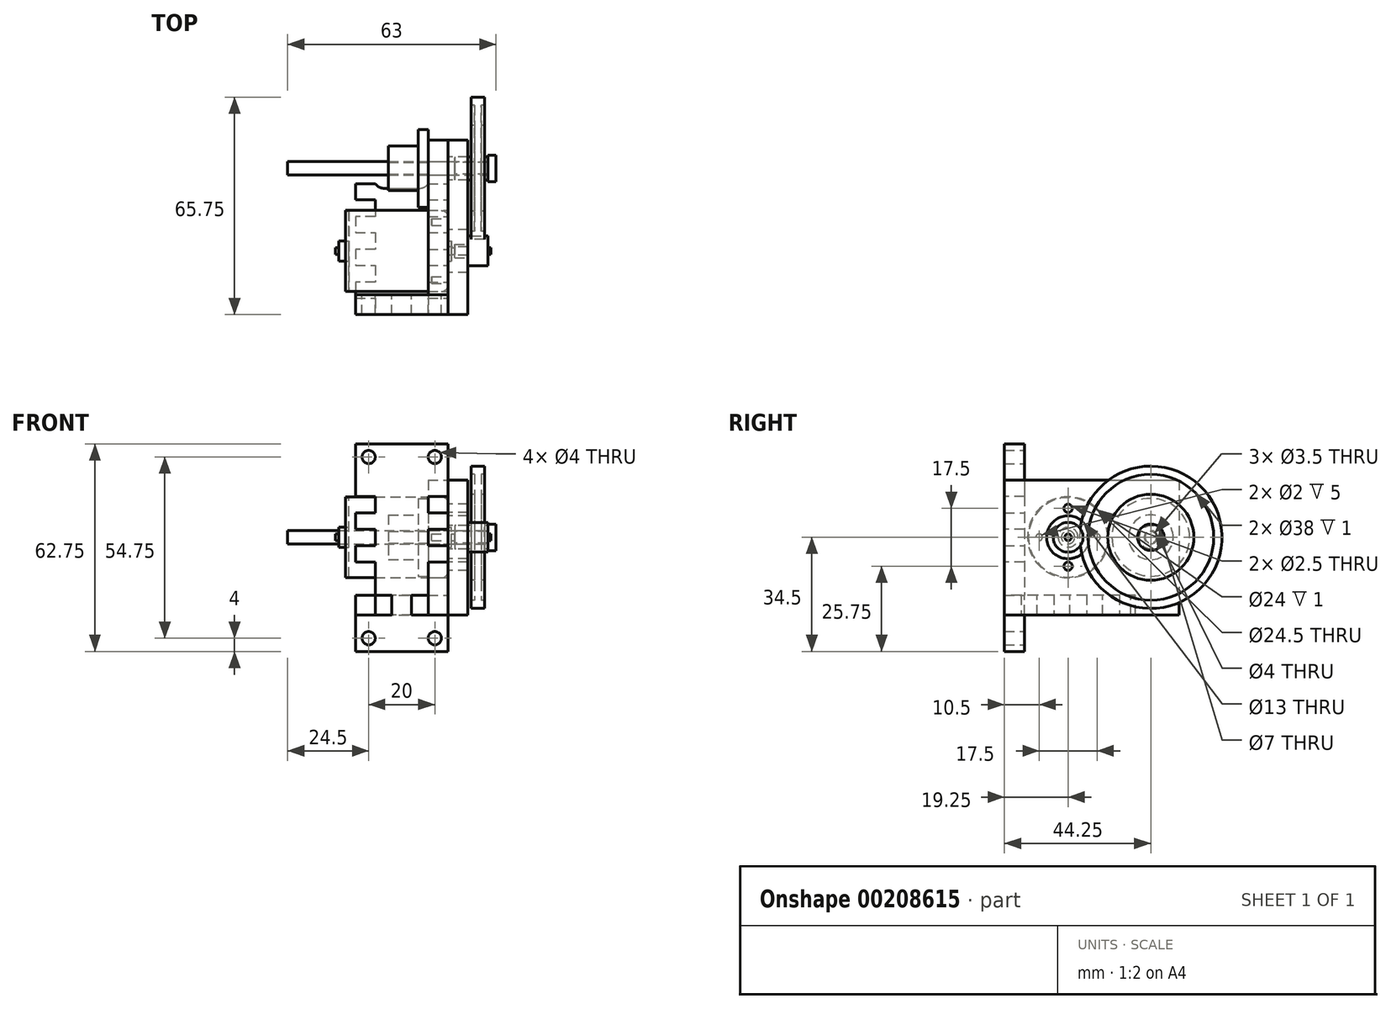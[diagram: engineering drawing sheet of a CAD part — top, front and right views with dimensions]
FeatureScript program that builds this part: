
annotation { "Feature Type Name" : "Feature", "Feature Type Description" : "" }
export const myFeature = defineFeature(function(context is Context, id is Id, definition is map)
    precondition{}
    {
        {
            assignVariable(context, id + "F0", {"name" : "ply", "anyValue" : 6});
        }
        {
            var Q0;
            Q0=qCreatedBy(makeId("Top.planeOp"),FACE);
            var sketch = newSketch(context, id + "F1", { "sketchPlane" : qUnion([Q0])});
            skLineSegment(sketch, "E0", {"start": v(0, 21.5) * mm, "end": v(2, 21.5) * mm});
            skLineSegment(sketch, "E1", {"start": v(2, 21.5) * mm, "end": v(2, 19) * mm});
            skLineSegment(sketch, "E2", {"start": v(2, 19) * mm, "end": v(1, 19) * mm});
            skLineSegment(sketch, "E3", {"start": v(1, 19) * mm, "end": v(1, 13) * mm});
            skLineSegment(sketch, "E4", {"start": v(1, 13) * mm, "end": v(2, 13) * mm});
            skLineSegment(sketch, "E5", {"start": v(2, 13) * mm, "end": v(2, 3.5) * mm});
            skLineSegment(sketch, "E6", {"start": v(2, 3.5) * mm, "end": v(3, 3.5) * mm});
            skLineSegment(sketch, "E7", {"start": v(3, 3.5) * mm, "end": v(3, 1.75) * mm});
            skLineSegment(sketch, "E8", {"start": v(3, 1.75) * mm, "end": v(0, 1.75) * mm});
            skLineSegment(sketch, "E9", {"start": v(0, 1.75) * mm, "end": v(0, 21.5) * mm, "construction": true});
            skLineSegment(sketch, "E10", {"start": v(0, 0) * mm, "end": v(6.26, 0) * mm, "construction": true});
            skLineSegment(sketch, "E11.MirrorCS", {"start": v(-7, 3.5) * mm, "end": v(-7, 1.75) * mm});
            skLineSegment(sketch, "E12.MirrorCS", {"start": v(0, 21.5) * mm, "end": v(-2, 21.5) * mm});
            skLineSegment(sketch, "E13.MirrorCS", {"start": v(-2, 21.5) * mm, "end": v(-2, 19) * mm});
            skLineSegment(sketch, "E14.MirrorCS", {"start": v(-2, 3.5) * mm, "end": v(-7, 3.5) * mm});
            skLineSegment(sketch, "E15.MirrorCS", {"start": v(-2, 19) * mm, "end": v(-1, 19) * mm});
            skLineSegment(sketch, "E16.MirrorCS", {"start": v(-2, 13) * mm, "end": v(-2, 3.5) * mm});
            skLineSegment(sketch, "E17.MirrorCS", {"start": v(-7, 1.75) * mm, "end": v(0, 1.75) * mm});
            skLineSegment(sketch, "E18.MirrorCS", {"start": v(-1, 19) * mm, "end": v(-1, 13) * mm});
            skLineSegment(sketch, "E19.MirrorCS", {"start": v(-1, 13) * mm, "end": v(-2, 13) * mm});
            skSolve(sketch);
        }
        {
            var Q0;
            Q0 = qSketchRegion(id + "F1", true);
            var Q1;
            Q1=sQuery(id+"F1.wireOp",EDGE,"E10");
            revolve(context, id + "F2", {"entities" : qUnion([Q0]), "axis" : qUnion([Q1]), "revolveType" : RevolveType.FULL});
        }
        {
            var Q0;
            Q0=qCreatedBy(makeId("Top.planeOp"),FACE);
            var sketch = newSketch(context, id + "F3", { "sketchPlane" : qUnion([Q0])});
            skLineSegment(sketch, "E20", {"start": v(-57.5, 2) * mm, "end": v(3, 2) * mm});
            skLineSegment(sketch, "E21", {"start": v(3, 2) * mm, "end": v(3, 4) * mm});
            skLineSegment(sketch, "E22", {"start": v(3, 4) * mm, "end": v(5.5, 4) * mm});
            skLineSegment(sketch, "E23", {"start": v(5.5, 4) * mm, "end": v(5.5, 0) * mm});
            skLineSegment(sketch, "E24", {"start": v(5.5, 0) * mm, "end": v(-57.5, 0) * mm});
            skLineSegment(sketch, "E25", {"start": v(-57.5, 0) * mm, "end": v(-57.5, 2) * mm});
            skSolve(sketch);
        }
        {
            var Q0;
            Q0 = qSketchRegion(id + "F3", true);
            var Q1;
            Q1=sQuery(id+"F3.wireOp",EDGE,"E24");
            revolve(context, id + "F4", {"entities" : qUnion([Q0]), "axis" : qUnion([Q1]), "revolveType" : RevolveType.FULL});
        }
        {
            var Q0;
            Q0=qCreatedBy(makeId("Top.planeOp"),FACE);
            var sketch = newSketch(context, id + "F5", { "sketchPlane" : qUnion([Q0])});
            skLineSegment(sketch, "E26", {"start": v(-40, -12.75) * mm, "end": v(-11, -12.75) * mm});
            skLineSegment(sketch, "E27", {"start": v(-9, -14.75) * mm, "end": v(-9, -22) * mm});
            skLineSegment(sketch, "E28", {"start": v(-9, -22) * mm, "end": v(-8, -22) * mm});
            skLineSegment(sketch, "E29", {"start": v(-8, -22) * mm, "end": v(-8, -24) * mm});
            skLineSegment(sketch, "E30", {"start": v(-8, -24) * mm, "end": v(-7, -24) * mm});
            skLineSegment(sketch, "E31", {"start": v(-3, -20.5) * mm, "end": v(3, -20.5) * mm});
            skLineSegment(sketch, "E32", {"start": v(3, -20.5) * mm, "end": v(3, -24) * mm});
            skLineSegment(sketch, "E33", {"start": v(3, -24) * mm, "end": v(4, -24) * mm});
            skLineSegment(sketch, "E34", {"start": v(4, -24) * mm, "end": v(4, -25) * mm});
            skLineSegment(sketch, "E35", {"start": v(4, -25) * mm, "end": v(-43, -25) * mm});
            skLineSegment(sketch, "E36", {"start": v(-43, -25) * mm, "end": v(-43, -24) * mm});
            skLineSegment(sketch, "E37", {"start": v(-43, -24) * mm, "end": v(-42, -24) * mm});
            skLineSegment(sketch, "E38", {"start": v(-42, -24) * mm, "end": v(-42, -22) * mm});
            skLineSegment(sketch, "E39", {"start": v(-42, -22) * mm, "end": v(-39, -22) * mm});
            skLineSegment(sketch, "E40", {"start": v(-39, -22) * mm, "end": v(-39, -13) * mm});
            skLineSegment(sketch, "E41", {"start": v(-39, -13) * mm, "end": v(-40, -13) * mm});
            skLineSegment(sketch, "E42", {"start": v(-40, -13) * mm, "end": v(-40, -12.75) * mm});
            skLineSegment(sketch, "E43", {"start": v(-7, -24) * mm, "end": v(-7, -23) * mm});
            skLineSegment(sketch, "E44", {"start": v(-7, -23) * mm, "end": v(-3, -23) * mm});
            skLineSegment(sketch, "E45", {"start": v(-3, -23) * mm, "end": v(-3, -20.5) * mm});
            skPoint(sketch, "E46.visualSharp", {"position": v(-9, -12.75) * mm});
            skArc(sketch, "E46.filletArc", {"start": v(-9, -14.75) * mm, "mid": v(-9.59, -13.34) * mm, "end": v(-11, -12.75) * mm});
            skLineSegment(sketch, "E47", {"start": v(0, -20.5) * mm, "end": v(0, -25) * mm, "construction": true});
            skSolve(sketch);
        }
        {
            var Q0;
            Q0 = qSketchRegion(id + "F5", true);
            var Q1;
            Q1=sQuery(id+"F5.wireOp",EDGE,"E35");
            revolve(context, id + "F6", {"entities" : qUnion([Q0]), "axis" : qUnion([Q1]), "revolveType" : RevolveType.FULL});
        }
        {
            var Q0;
            Q0=makeQuery(id+"F6.opRevolve","SWEPT_FACE",FACE,{"disambiguationData":[OSD([sQuery(id+"F5.wireOp",EDGE,"E27")])]});
            var sketch = newSketch(context, id + "F7", { "sketchPlane" : qUnion([Q0])});
            skLineSegment(sketch, "E48", {"start": v(-25, 0) * mm, "end": v(-33.75, 0) * mm, "construction": true});
            skLineSegment(sketch, "E49", {"start": v(-25, 0) * mm, "end": v(-25, 4.03) * mm, "construction": true});
            skCircle(sketch, "E50", {"center": v(-33.75, 0) * mm, "radius": 1 * mm});
            skCircle(sketch, "E51.MirrorC", {"center": v(-16.25, 0) * mm, "radius": 1 * mm});
            skSolve(sketch);
        }
        {
            var Q0;
            Q0 = qSketchRegion(id + "F7", true);
            extrude(context, id + "F8", {"entities" : qUnion([Q0]), "operationType" : NewBodyOperationType.REMOVE, "oppositeDirection" : true, "depth" : 5 * mm});
        }
        {
            var Q0;
            Q0=makeQuery(id+"F6.opRevolve","SWEPT_FACE",FACE,{"disambiguationData":[OSD([sQuery(id+"F5.wireOp",EDGE,"E27")])]});
            var sketch = newSketch(context, id + "F9", { "sketchPlane" : qUnion([Q0])});
            skCircle(sketch, "E52", {"center": v(-25, 0) * mm, "radius": 6.5 * mm});
            skLineSegment(sketch, "E53.bottom", {"start": v(-44.25, 17.25) * mm, "end": v(8.5, 17.25) * mm});
            skLineSegment(sketch, "E53.top", {"start": v(-44.25, -23.5) * mm, "end": v(8.5, -23.5) * mm});
            skLineSegment(sketch, "E53.left", {"start": v(-44.25, 17.25) * mm, "end": v(-44.25, -23.5) * mm});
            skLineSegment(sketch, "E53.right", {"start": v(8.5, 17.25) * mm, "end": v(8.5, -23.5) * mm});
            skCircle(sketch, "E54", {"center": v(0, 0) * mm, "radius": 3.5 * mm});
            skCircle(sketch, "E55", {"center": v(-25, 8.75) * mm, "radius": 1.25 * mm});
            skCircle(sketch, "E56", {"center": v(-25, -8.75) * mm, "radius": 1.25 * mm});
            skLineSegment(sketch, "E57", {"start": v(-25, 0) * mm, "end": v(-33.75, 0) * mm, "construction": true});
            skLineSegment(sketch, "E58", {"start": v(-25, 0) * mm, "end": v(-25, 8.75) * mm, "construction": true});
            skLineSegment(sketch, "E59", {"start": v(-25, 0) * mm, "end": v(-25, -8.75) * mm, "construction": true});
            skSolve(sketch);
        }
        {
            var Q0;
            Q0 = qSketchRegion(id + "F9", true);
            extrude(context, id + "F10", {"entities" : qUnion([Q0]), "depth" : (getVariable(context, 'ply')) * mm});
        }
        {
            var Q0;
            Q0=makeQuery(id+"F10.opExtrude","CAP_FACE",FACE,{"disambiguationData":[OSD([sQuery(id+"F9.wireOp",EDGE,"E52"),sQuery(id+"F9.wireOp",EDGE,"E53.bottom"),sQuery(id+"F9.wireOp",EDGE,"E53.top"),sQuery(id+"F9.wireOp",EDGE,"E53.left"),sQuery(id+"F9.wireOp",EDGE,"E53.right"),sQuery(id+"F9.wireOp",EDGE,"E54"),sQuery(id+"F9.wireOp",EDGE,"E55"),sQuery(id+"F9.wireOp",EDGE,"e99d51b7-512e-4ea6-ba02-21552ba813760.MirrorC"),sQuery(id+"F9.wireOp",EDGE,"rxjcsG1S-Jmm9-2wk5-1xT8-CNA6QqetSPPh"),sQuery(id+"F9.wireOp",EDGE,"21b3dd45-f856-45b4-8939-340bf7965a580.MirrorC"),sQuery(id+"F9.wireOp",EDGE,"IxMQc4Ss-w2DJ-x6JC-kdgd-lpgZtMJqyD3m"),sQuery(id+"F9.wireOp",EDGE,"a0a60418-0544-418f-8943-292dfd96fc9f0.MirrorC")])],"isStart":true});
            var sketch = newSketch(context, id + "F11", { "sketchPlane" : qUnion([Q0])});
            skLineSegment(sketch, "E60.top", {"start": v(-8.5, -23.5) * mm, "end": v(44.25, -23.5) * mm, "construction": true});
            skLineSegment(sketch, "E60.left", {"start": v(-8.5, 17.25) * mm, "end": v(-8.5, -23.5) * mm});
            skCircle(sketch, "E61", {"center": v(0, 0) * mm, "radius": 2 * mm});
            skCircle(sketch, "E62", {"center": v(25, 0) * mm, "radius": 12.25 * mm});
            skLineSegment(sketch, "E63", {"start": v(-8.5, -23.5) * mm, "end": v(4.65, -23.5) * mm});
            skLineSegment(sketch, "E64", {"start": v(4.65, -23.5) * mm, "end": v(4.65, -17.5) * mm});
            skLineSegment(sketch, "E65", {"start": v(4.65, -17.5) * mm, "end": v(9.55, -17.5) * mm});
            skLineSegment(sketch, "E66", {"start": v(9.55, -17.5) * mm, "end": v(9.55, -23.5) * mm});
            skLineSegment(sketch, "E67", {"start": v(9.55, -23.5) * mm, "end": v(14.55, -23.5) * mm});
            skLineSegment(sketch, "E68.1.0.0", {"start": v(14.55, -17.5) * mm, "end": v(19.45, -17.5) * mm});
            skLineSegment(sketch, "E68.1.0.1", {"start": v(14.55, -23.5) * mm, "end": v(14.55, -17.5) * mm});
            skLineSegment(sketch, "E68.1.0.2", {"start": v(19.45, -23.5) * mm, "end": v(24.45, -23.5) * mm});
            skLineSegment(sketch, "E68.1.0.3", {"start": v(19.45, -17.5) * mm, "end": v(19.45, -23.5) * mm});
            skLineSegment(sketch, "E68.2.0.0", {"start": v(24.45, -17.5) * mm, "end": v(29.35, -17.5) * mm});
            skLineSegment(sketch, "E68.2.0.1", {"start": v(24.45, -23.5) * mm, "end": v(24.45, -17.5) * mm});
            skLineSegment(sketch, "E68.2.0.2", {"start": v(29.35, -23.5) * mm, "end": v(34.35, -23.5) * mm});
            skLineSegment(sketch, "E68.2.0.3", {"start": v(29.35, -17.5) * mm, "end": v(29.35, -23.5) * mm});
            skLineSegment(sketch, "E68.direction1", {"start": v(4.65, -23.5) * mm, "end": v(14.55, -23.5) * mm, "construction": true});
            skLineSegment(sketch, "E69.0.3.0", {"start": v(34.35, -17.5) * mm, "end": v(39.25, -17.5) * mm});
            skLineSegment(sketch, "E69.3.3.0", {"start": v(34.35, -23.5) * mm, "end": v(34.35, -17.5) * mm});
            skLineSegment(sketch, "E69.6.3.0", {"start": v(39.25, -23.5) * mm, "end": v(44.25, -23.5) * mm});
            skLineSegment(sketch, "E69.9.3.0", {"start": v(39.25, -17.5) * mm, "end": v(39.25, -23.5) * mm});
            skLineSegment(sketch, "E70", {"start": v(38.25, 17.25) * mm, "end": v(38.25, 12.35) * mm});
            skLineSegment(sketch, "E71", {"start": v(38.25, 12.35) * mm, "end": v(44.25, 12.35) * mm});
            skLineSegment(sketch, "E72", {"start": v(44.25, 12.35) * mm, "end": v(44.25, 7.35) * mm});
            skLineSegment(sketch, "E73", {"start": v(44.25, 7.35) * mm, "end": v(38.25, 7.35) * mm});
            skLineSegment(sketch, "E74", {"start": v(38.25, 7.35) * mm, "end": v(38.25, 2.45) * mm});
            skLineSegment(sketch, "E75", {"start": v(38.25, 2.45) * mm, "end": v(44.25, 2.45) * mm});
            skLineSegment(sketch, "E76", {"start": v(44.25, 2.45) * mm, "end": v(44.25, -2.55) * mm});
            skLineSegment(sketch, "E77", {"start": v(44.25, -2.55) * mm, "end": v(38.25, -2.55) * mm});
            skLineSegment(sketch, "E78", {"start": v(38.25, -2.55) * mm, "end": v(38.25, -7.45) * mm});
            skLineSegment(sketch, "E79", {"start": v(38.25, -7.45) * mm, "end": v(44.25, -7.45) * mm});
            skLineSegment(sketch, "E80", {"start": v(44.25, -7.45) * mm, "end": v(44.25, -23.5) * mm});
            skLineSegment(sketch, "E81", {"start": v(38.25, 17.25) * mm, "end": v(-8.5, 17.25) * mm});
            skSolve(sketch);
        }
        {
            var Q0;
            Q0 = qSketchRegion(id + "F11", true);
            extrude(context, id + "F12", {"entities" : qUnion([Q0]), "depth" : (getVariable(context, 'ply')) * mm});
        }
        {
            var Q0;
            Q0=makeQuery(id+"F12.opExtrude","SWEPT_FACE",FACE,{"disambiguationData":[OSD([sQuery(id+"F11.wireOp",EDGE,"E65")])]});
            var sketch = newSketch(context, id + "F13", { "sketchPlane" : qUnion([Q0])});
            skLineSegment(sketch, "E82", {"start": v(-9, 4.65) * mm, "end": v(-9, 9.55) * mm});
            skLineSegment(sketch, "E83", {"start": v(-9, 9.55) * mm, "end": v(-15, 9.55) * mm});
            skLineSegment(sketch, "E84", {"start": v(-15, 9.55) * mm, "end": v(-15, 14.55) * mm});
            skLineSegment(sketch, "E85", {"start": v(-15, 14.55) * mm, "end": v(-9, 14.55) * mm});
            skLineSegment(sketch, "E86", {"start": v(-9, 14.55) * mm, "end": v(-9, 19.45) * mm});
            skLineSegment(sketch, "E87", {"start": v(-9, 19.45) * mm, "end": v(-15, 19.45) * mm});
            skLineSegment(sketch, "E88", {"start": v(-15, 19.45) * mm, "end": v(-15, 24.45) * mm});
            skLineSegment(sketch, "E89", {"start": v(-15, 24.45) * mm, "end": v(-9, 24.45) * mm});
            skLineSegment(sketch, "E90", {"start": v(-9, 24.45) * mm, "end": v(-9, 29.35) * mm});
            skLineSegment(sketch, "E91", {"start": v(-9, 29.35) * mm, "end": v(-15, 29.35) * mm});
            skLineSegment(sketch, "E92", {"start": v(-15, 29.35) * mm, "end": v(-15, 34.35) * mm});
            skLineSegment(sketch, "E93", {"start": v(-15, 34.35) * mm, "end": v(-9, 34.35) * mm});
            skLineSegment(sketch, "E94", {"start": v(-9, 34.35) * mm, "end": v(-9, 39.25) * mm});
            skLineSegment(sketch, "E95", {"start": v(-9, 39.25) * mm, "end": v(-15, 39.25) * mm});
            skLineSegment(sketch, "E96", {"start": v(-15, 39.25) * mm, "end": v(-15, 44.25) * mm});
            skLineSegment(sketch, "E97", {"start": v(-23, 44.25) * mm, "end": v(-23, 3.5) * mm, "construction": true});
            skLineSegment(sketch, "E98", {"start": v(-15, 4.65) * mm, "end": v(-15, 4.65) * mm});
            skLineSegment(sketch, "E99", {"start": v(-17.53, 6.04) * mm, "end": v(-23, 6.04) * mm});
            skLineSegment(sketch, "E100", {"start": v(-15, 4.65) * mm, "end": v(-9, 4.65) * mm});
            skLineSegment(sketch, "E101.MirrorCS", {"start": v(-37, 39.25) * mm, "end": v(-31, 39.25) * mm});
            skLineSegment(sketch, "E102.MirrorCS", {"start": v(-31, 39.25) * mm, "end": v(-31, 44.25) * mm});
            skLineSegment(sketch, "E103.MirrorCS", {"start": v(-37, 4.65) * mm, "end": v(-37, 9.55) * mm});
            skLineSegment(sketch, "E104.MirrorCS", {"start": v(-37, 9.55) * mm, "end": v(-31, 9.55) * mm});
            skLineSegment(sketch, "E105.MirrorCS", {"start": v(-31, 9.55) * mm, "end": v(-31, 14.55) * mm});
            skLineSegment(sketch, "E106.MirrorCS", {"start": v(-31, 14.55) * mm, "end": v(-37, 14.55) * mm});
            skLineSegment(sketch, "E107.MirrorCS", {"start": v(-37, 14.55) * mm, "end": v(-37, 19.45) * mm});
            skLineSegment(sketch, "E108.MirrorCS", {"start": v(-37, 29.35) * mm, "end": v(-31, 29.35) * mm});
            skLineSegment(sketch, "E109.MirrorCS", {"start": v(-37, 24.45) * mm, "end": v(-37, 29.35) * mm});
            skLineSegment(sketch, "E110.MirrorCS", {"start": v(-31, 24.45) * mm, "end": v(-37, 24.45) * mm});
            skLineSegment(sketch, "E111.MirrorCS", {"start": v(-37, 19.45) * mm, "end": v(-31, 19.45) * mm});
            skLineSegment(sketch, "E112.MirrorCS", {"start": v(-31, 29.35) * mm, "end": v(-31, 34.35) * mm});
            skLineSegment(sketch, "E113.MirrorCS", {"start": v(-31, 4.65) * mm, "end": v(-37, 4.65) * mm});
            skLineSegment(sketch, "E114.MirrorCS", {"start": v(-31, 19.45) * mm, "end": v(-31, 24.45) * mm});
            skLineSegment(sketch, "E115.MirrorCS", {"start": v(-28.47, 6.04) * mm, "end": v(-23, 6.04) * mm});
            skLineSegment(sketch, "E116.MirrorCS", {"start": v(-31, 34.35) * mm, "end": v(-37, 34.35) * mm});
            skLineSegment(sketch, "E117.MirrorCS", {"start": v(-37, 34.35) * mm, "end": v(-37, 39.25) * mm});
            skLineSegment(sketch, "E118.MirrorCS", {"start": v(-31, 4.65) * mm, "end": v(-31, 4.65) * mm});
            skLineSegment(sketch, "E119", {"start": v(-20, 44.25) * mm, "end": v(-20, 38.25) * mm});
            skLineSegment(sketch, "E120", {"start": v(-20, 44.25) * mm, "end": v(-15, 44.25) * mm});
            skLineSegment(sketch, "E121.MirrorCS", {"start": v(-26, 44.25) * mm, "end": v(-26, 38.25) * mm});
            skLineSegment(sketch, "E122.MirrorCS", {"start": v(-26, 44.25) * mm, "end": v(-31, 44.25) * mm});
            skLineSegment(sketch, "E123", {"start": v(-20, 38.25) * mm, "end": v(-26, 38.25) * mm});
            skPoint(sketch, "E124.visualSharp", {"position": v(-30.12, 6.04) * mm});
            skArc(sketch, "E124.filletArc", {"start": v(-28.47, 6.04) * mm, "mid": v(-29.91, 5.67) * mm, "end": v(-31, 4.65) * mm});
            skPoint(sketch, "E125.visualSharp", {"position": v(-15.88, 6.04) * mm});
            skArc(sketch, "E125.filletArc", {"start": v(-15, 4.65) * mm, "mid": v(-16.09, 5.67) * mm, "end": v(-17.53, 6.04) * mm});
            skSolve(sketch);
        }
        {
            var Q0;
            Q0 = qSketchRegion(id + "F13", true);
            extrude(context, id + "F14", {"entities" : qUnion([Q0]), "depth" : (getVariable(context, 'ply')) * mm});
        }
        {
            var Q0;
            Q0=makeQuery(id+"F14.opExtrude","SWEPT_FACE",FACE,{"disambiguationData":[OSD([sQuery(id+"F13.wireOp",EDGE,"E123")])]});
            var sketch = newSketch(context, id + "F15", { "sketchPlane" : qUnion([Q0])});
            skLineSegment(sketch, "E126", {"start": v(-9, 28.25) * mm, "end": v(-9, 12.35) * mm});
            skLineSegment(sketch, "E127", {"start": v(-9, 12.35) * mm, "end": v(-15, 12.35) * mm});
            skLineSegment(sketch, "E128", {"start": v(-15, 12.35) * mm, "end": v(-15, 7.35) * mm});
            skLineSegment(sketch, "E129", {"start": v(-15, 7.35) * mm, "end": v(-9, 7.35) * mm});
            skLineSegment(sketch, "E130", {"start": v(-9, 7.35) * mm, "end": v(-9, 2.45) * mm});
            skLineSegment(sketch, "E131", {"start": v(-9, 2.45) * mm, "end": v(-15, 2.45) * mm});
            skLineSegment(sketch, "E132", {"start": v(-15, 2.45) * mm, "end": v(-15, -2.55) * mm});
            skLineSegment(sketch, "E133", {"start": v(-15, -2.55) * mm, "end": v(-9, -2.55) * mm});
            skLineSegment(sketch, "E134", {"start": v(-9, -2.55) * mm, "end": v(-9, -7.45) * mm});
            skLineSegment(sketch, "E135", {"start": v(-9, -7.45) * mm, "end": v(-15, -7.45) * mm});
            skLineSegment(sketch, "E136", {"start": v(-15, -7.45) * mm, "end": v(-15, -17.5) * mm});
            skLineSegment(sketch, "E137", {"start": v(-15, -17.5) * mm, "end": v(-20, -17.5) * mm});
            skLineSegment(sketch, "E138", {"start": v(-20, -17.5) * mm, "end": v(-20, -23.5) * mm});
            skLineSegment(sketch, "E139", {"start": v(-20, -23.5) * mm, "end": v(-9, -23.5) * mm});
            skLineSegment(sketch, "E140", {"start": v(-9, -23.5) * mm, "end": v(-9, -34.5) * mm});
            skLineSegment(sketch, "E141", {"start": v(-9, -34.5) * mm, "end": v(-23, -34.5) * mm});
            skLineSegment(sketch, "E142", {"start": v(-23, -34.5) * mm, "end": v(-23, 28.25) * mm, "construction": true});
            skLineSegment(sketch, "E143", {"start": v(-9, 28.25) * mm, "end": v(-23, 28.25) * mm});
            skLineSegment(sketch, "E144.MirrorCS", {"start": v(-37, 28.25) * mm, "end": v(-37, 12.35) * mm});
            skLineSegment(sketch, "E145.MirrorCS", {"start": v(-31, 7.35) * mm, "end": v(-37, 7.35) * mm});
            skLineSegment(sketch, "E146.MirrorCS", {"start": v(-37, 12.35) * mm, "end": v(-31, 12.35) * mm});
            skLineSegment(sketch, "E147.MirrorCS", {"start": v(-37, -34.5) * mm, "end": v(-23, -34.5) * mm});
            skLineSegment(sketch, "E148.MirrorCS", {"start": v(-37, 28.25) * mm, "end": v(-23, 28.25) * mm});
            skLineSegment(sketch, "E149.MirrorCS", {"start": v(-31, 12.35) * mm, "end": v(-31, 7.35) * mm});
            skLineSegment(sketch, "E150.MirrorCS", {"start": v(-31, 2.45) * mm, "end": v(-31, -2.55) * mm});
            skLineSegment(sketch, "E151.MirrorCS", {"start": v(-31, -7.45) * mm, "end": v(-31, -17.5) * mm});
            skLineSegment(sketch, "E152.MirrorCS", {"start": v(-31, -17.5) * mm, "end": v(-26, -17.5) * mm});
            skLineSegment(sketch, "E153.MirrorCS", {"start": v(-31, -2.55) * mm, "end": v(-37, -2.55) * mm});
            skLineSegment(sketch, "E154.MirrorCS", {"start": v(-26, -17.5) * mm, "end": v(-26, -23.5) * mm});
            skLineSegment(sketch, "E155.MirrorCS", {"start": v(-37, 2.45) * mm, "end": v(-31, 2.45) * mm});
            skLineSegment(sketch, "E156.MirrorCS", {"start": v(-37, -23.5) * mm, "end": v(-37, -34.5) * mm});
            skLineSegment(sketch, "E157.MirrorCS", {"start": v(-26, -23.5) * mm, "end": v(-37, -23.5) * mm});
            skLineSegment(sketch, "E158.MirrorCS", {"start": v(-37, -7.45) * mm, "end": v(-31, -7.45) * mm});
            skLineSegment(sketch, "E159.MirrorCS", {"start": v(-37, 7.35) * mm, "end": v(-37, 2.45) * mm});
            skLineSegment(sketch, "E160.MirrorCS", {"start": v(-37, -2.55) * mm, "end": v(-37, -7.45) * mm});
            skCircle(sketch, "E161", {"center": v(-33, 24.25) * mm, "radius": 2 * mm});
            skCircle(sketch, "E162", {"center": v(-13, 24.25) * mm, "radius": 2 * mm});
            skCircle(sketch, "E163", {"center": v(-33, -30.5) * mm, "radius": 2 * mm});
            skCircle(sketch, "E164", {"center": v(-13, -30.5) * mm, "radius": 2 * mm});
            skSolve(sketch);
        }
        {
            var Q0;
            Q0 = qSketchRegion(id + "F15", true);
            extrude(context, id + "F16", {"entities" : qUnion([Q0]), "depth" : (getVariable(context, 'ply')) * mm});
        }
        {
            var Q0;
            Q0=makeQuery(id+"F12.opExtrude","CAP_FACE",FACE,{"disambiguationData":[OSD([sQuery(id+"F11.wireOp",EDGE,"E60.left"),sQuery(id+"F11.wireOp",EDGE,"E61"),sQuery(id+"F11.wireOp",EDGE,"E62"),sQuery(id+"F11.wireOp",EDGE,"E63"),sQuery(id+"F11.wireOp",EDGE,"E64"),sQuery(id+"F11.wireOp",EDGE,"E65"),sQuery(id+"F11.wireOp",EDGE,"E66"),sQuery(id+"F11.wireOp",EDGE,"E67"),sQuery(id+"F11.wireOp",EDGE,"E68.1.0.0"),sQuery(id+"F11.wireOp",EDGE,"E68.1.0.1"),sQuery(id+"F11.wireOp",EDGE,"E68.1.0.2"),sQuery(id+"F11.wireOp",EDGE,"E68.1.0.3"),sQuery(id+"F11.wireOp",EDGE,"E68.2.0.0"),sQuery(id+"F11.wireOp",EDGE,"E68.2.0.1"),sQuery(id+"F11.wireOp",EDGE,"E68.2.0.2"),sQuery(id+"F11.wireOp",EDGE,"E68.2.0.3"),sQuery(id+"F11.wireOp",EDGE,"E69.0.3.0"),sQuery(id+"F11.wireOp",EDGE,"E69.3.3.0"),sQuery(id+"F11.wireOp",EDGE,"E69.6.3.0"),sQuery(id+"F11.wireOp",EDGE,"E69.9.3.0"),sQuery(id+"F11.wireOp",EDGE,"E70"),sQuery(id+"F11.wireOp",EDGE,"E71"),sQuery(id+"F11.wireOp",EDGE,"E72"),sQuery(id+"F11.wireOp",EDGE,"E73"),sQuery(id+"F11.wireOp",EDGE,"E74"),sQuery(id+"F11.wireOp",EDGE,"E75"),sQuery(id+"F11.wireOp",EDGE,"E76"),sQuery(id+"F11.wireOp",EDGE,"E77"),sQuery(id+"F11.wireOp",EDGE,"E78"),sQuery(id+"F11.wireOp",EDGE,"E79"),sQuery(id+"F11.wireOp",EDGE,"E80"),sQuery(id+"F11.wireOp",EDGE,"E81")])],"isStart":false});
            var sketch = newSketch(context, id + "F17", { "sketchPlane" : qUnion([Q0])});
            skCircle(sketch, "E165", {"center": v(0, 0) * mm, "radius": 1.75 * mm});
            skCircle(sketch, "E166", {"center": v(0, 0) * mm, "radius": 11.75 * mm});
            skSolve(sketch);
        }
        {
            var Q0;
            Q0 = qSketchRegion(id + "F17", true);
            extrude(context, id + "F18", {"entities" : qUnion([Q0]), "depth" : 3 * mm});
        }
        {
            var Q0;
            Q0=makeQuery(id+"F18.opExtrude","CAP_FACE",FACE,{"disambiguationData":[OSD([sQuery(id+"F17.wireOp",EDGE,"E165"),sQuery(id+"F17.wireOp",EDGE,"E166")])],"isStart":false});
            var sketch = newSketch(context, id + "F19", { "sketchPlane" : qUnion([Q0])});
            skCircle(sketch, "E167", {"center": v(0, 0) * mm, "radius": 1.75 * mm});
            skCircle(sketch, "E168", {"center": v(0, 0) * mm, "radius": 6.75 * mm});
            skSolve(sketch);
        }
        {
            var Q0;
            Q0 = qSketchRegion(id + "F19", true);
            extrude(context, id + "F20", {"entities" : qUnion([Q0]), "depth" : 9 * mm});
        }
    });
